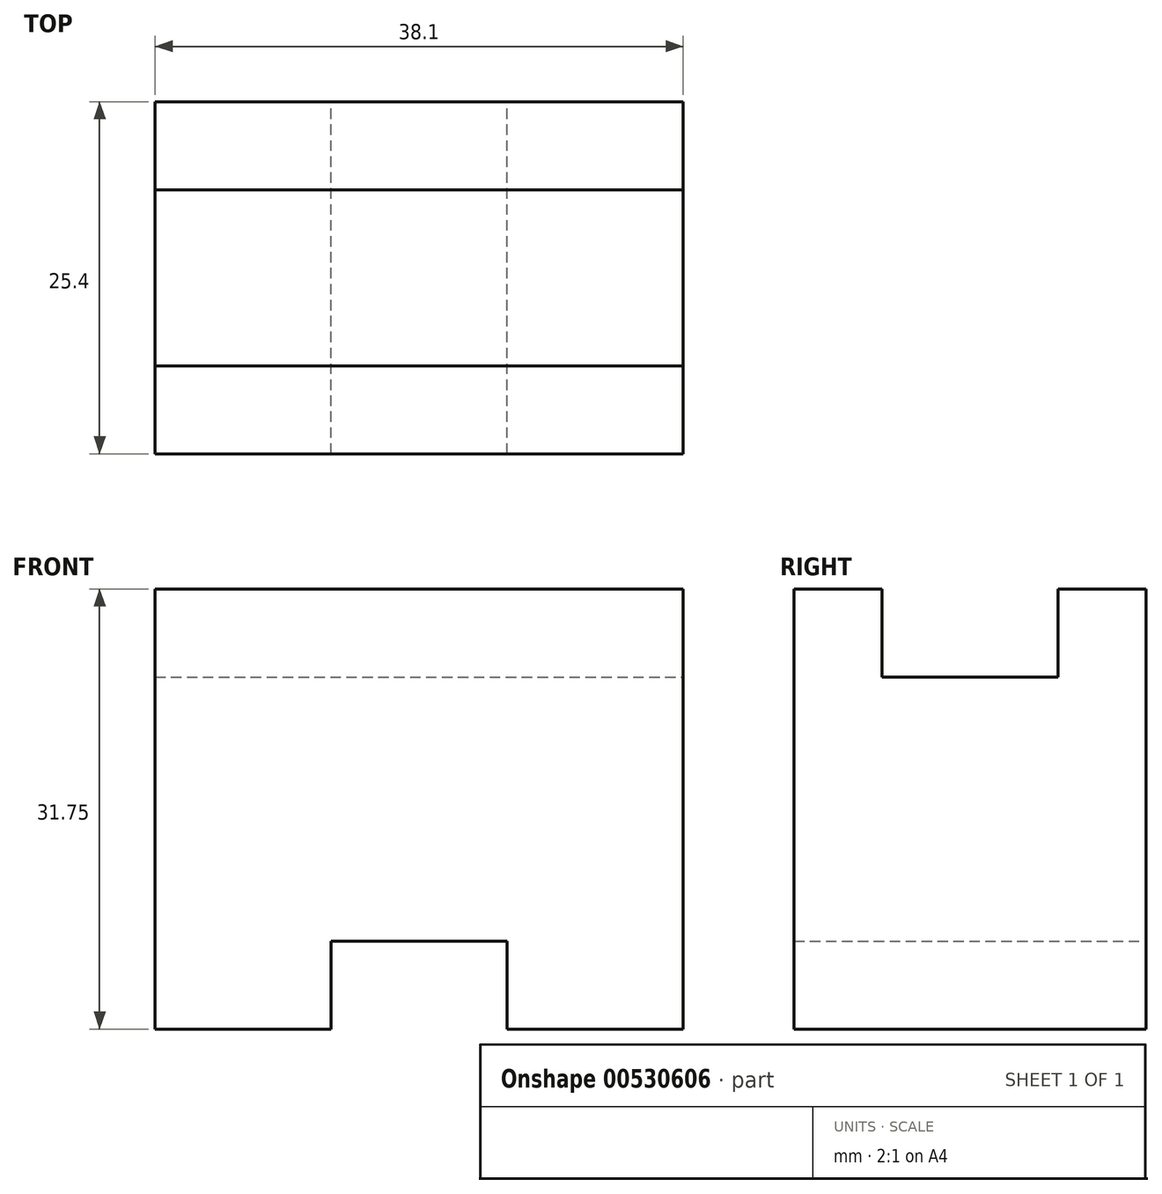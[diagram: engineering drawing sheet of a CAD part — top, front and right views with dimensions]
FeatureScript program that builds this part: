
annotation { "Feature Type Name" : "Feature", "Feature Type Description" : "" }
export const myFeature = defineFeature(function(context is Context, id is Id, definition is map)
    precondition{}
    {
        {
            var Q0;
            Q0=qCreatedBy(makeId("Front.planeOp"),FACE);
            var sketch = newSketch(context, id + "F0", { "sketchPlane" : qUnion([Q0])});
            skLineSegment(sketch, "E0", {"start": v(11.78, 31.66) * mm, "end": v(11.78, -0.1) * mm});
            skLineSegment(sketch, "E1", {"start": v(11.78, -0.1) * mm, "end": v(24.48, -0.1) * mm});
            skLineSegment(sketch, "E2", {"start": v(24.48, -0.1) * mm, "end": v(24.48, 6.26) * mm});
            skLineSegment(sketch, "E3", {"start": v(24.48, 6.26) * mm, "end": v(37.18, 6.26) * mm});
            skLineSegment(sketch, "E4", {"start": v(37.18, 6.26) * mm, "end": v(37.18, -0.1) * mm});
            skLineSegment(sketch, "E5", {"start": v(37.18, -0.1) * mm, "end": v(49.88, -0.1) * mm});
            skLineSegment(sketch, "E6", {"start": v(49.88, -0.1) * mm, "end": v(49.88, 31.66) * mm});
            skLineSegment(sketch, "E7", {"start": v(49.88, 31.66) * mm, "end": v(11.78, 31.66) * mm});
            skSolve(sketch);
        }
        {
            var Q0;
            Q0 = qSketchRegion(id + "F0", true);
            extrude(context, id + "F1", {"entities" : qUnion([Q0]), "depth" : 25.4 * mm, "offsetDistance" : 25.4 * mm});
        }
        {
            var Q0;
            Q0=makeQuery(id+"F1.opExtrude","SWEPT_FACE",FACE,{"disambiguationData":[OSD([sQuery(id+"F0.wireOp",EDGE,"E6")])]});
            var sketch = newSketch(context, id + "F2", { "sketchPlane" : qUnion([Q0])});
            skLineSegment(sketch, "E8", {"start": v(-19.05, 31.66) * mm, "end": v(-19.05, 25.3) * mm});
            skLineSegment(sketch, "E9", {"start": v(-19.05, 25.3) * mm, "end": v(-6.35, 25.3) * mm});
            skLineSegment(sketch, "E10", {"start": v(-6.35, 25.3) * mm, "end": v(-6.35, 31.66) * mm});
            skSolve(sketch);
        }
        {
            var Q0;
            Q0 = qSketchRegion(id + "F2", true);
            var Q1;
            {var subQ0=sQuery(id+"F2.wireOp",EDGE,"E8");Q1=makeQuery(id+"F2.imprint","IMPRINT",FACE,{"disambiguationData":[TD([[makeQuery(id+"F2.imprint","IMPRINT",EDGE,{"derivedFrom":subQ0}),1.0]])]});}
            extrude(context, id + "F3", {"entities" : qUnion([Q0, Q1]), "operationType" : NewBodyOperationType.REMOVE, "endBound" : BoundingType.THROUGH_ALL, "oppositeDirection" : true, "depth" : 38.1 * mm, "offsetDistance" : 25.4 * mm});
        }
    });
